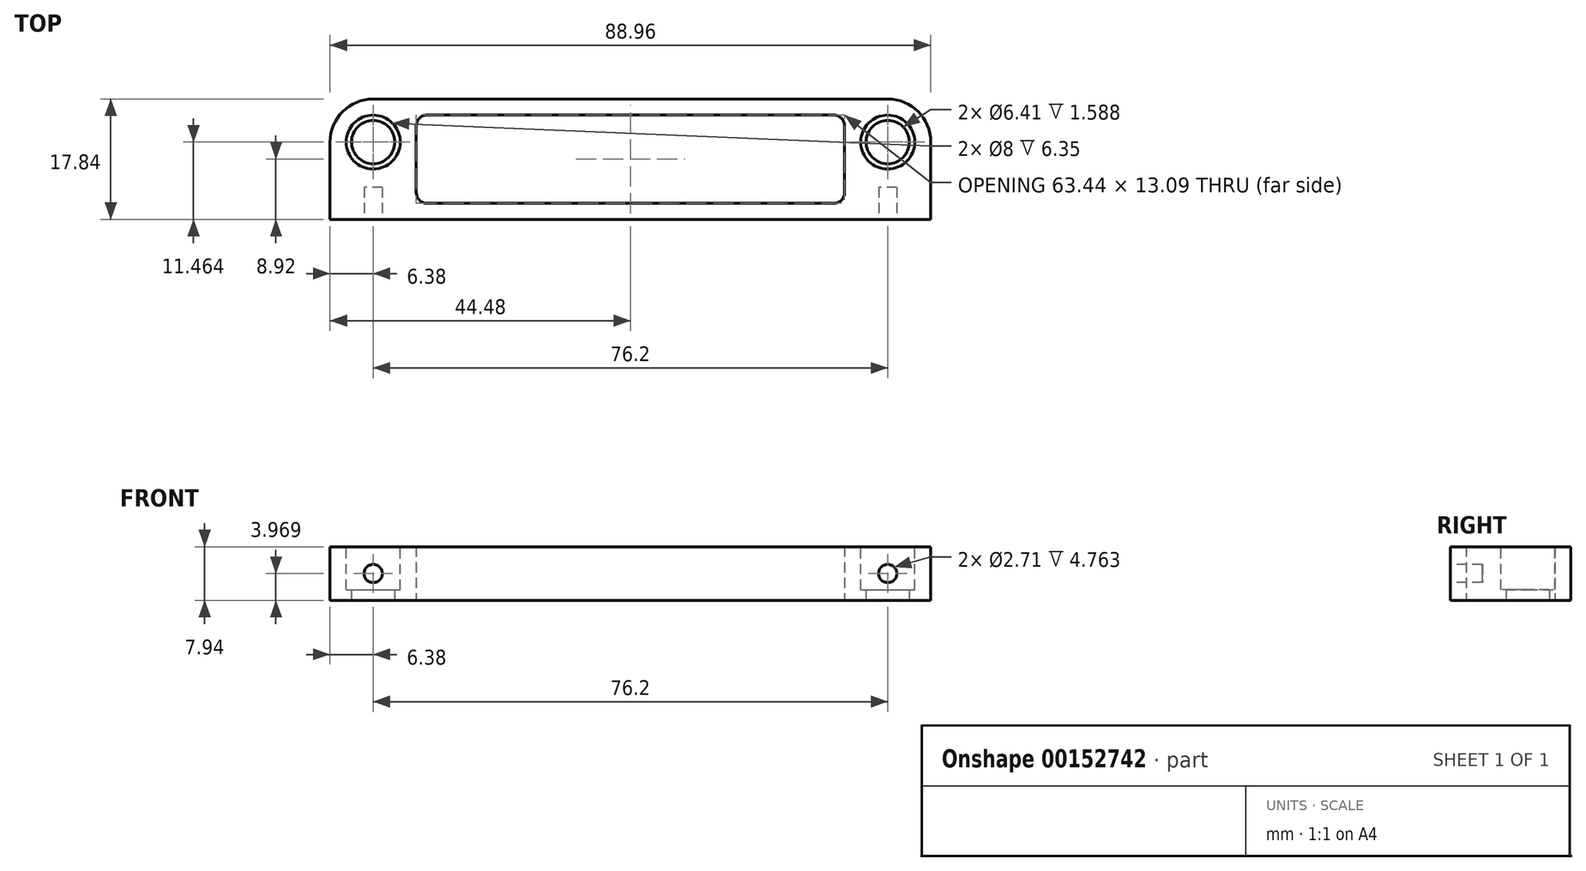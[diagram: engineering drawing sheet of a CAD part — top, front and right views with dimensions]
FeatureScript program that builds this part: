
annotation { "Feature Type Name" : "Feature", "Feature Type Description" : "" }
export const myFeature = defineFeature(function(context is Context, id is Id, definition is map)
    precondition{}
    {
        {
            var Q0;
            Q0=qCreatedBy(makeId("Top.planeOp"),FACE);
            var sketch = newSketch(context, id + "F0", { "sketchPlane" : qUnion([Q0])});
            skLineSegment(sketch, "E0.bottom", {"start": v(44.48, -8.92) * mm, "end": v(-44.48, -8.92) * mm});
            skLineSegment(sketch, "E0.top", {"start": v(44.48, 8.92) * mm, "end": v(-44.48, 8.92) * mm});
            skLineSegment(sketch, "E0.left", {"start": v(44.48, -8.92) * mm, "end": v(44.48, 8.92) * mm});
            skLineSegment(sketch, "E0.right", {"start": v(-44.48, -8.92) * mm, "end": v(-44.48, 8.92) * mm});
            skPoint(sketch, "E0.middle", {"position": v(0, 0) * mm});
            skLineSegment(sketch, "E1.bottom", {"start": v(31.72, -6.54) * mm, "end": v(-31.72, -6.54) * mm});
            skLineSegment(sketch, "E1.top", {"start": v(31.72, 6.54) * mm, "end": v(-31.72, 6.54) * mm});
            skLineSegment(sketch, "E1.left", {"start": v(31.72, -6.54) * mm, "end": v(31.72, 6.54) * mm});
            skLineSegment(sketch, "E1.right", {"start": v(-31.72, -6.54) * mm, "end": v(-31.72, 6.54) * mm});
            skLineSegment(sketch, "E2", {"start": v(44.48, 2.54) * mm, "end": v(38.1, 2.54) * mm, "construction": true});
            skLineSegment(sketch, "E3", {"start": v(38.1, 2.54) * mm, "end": v(38.1, 8.92) * mm, "construction": true});
            skCircle(sketch, "E4", {"center": v(38.1, 2.54) * mm, "radius": 3.2 * mm});
            skLineSegment(sketch, "E5", {"start": v(-44.48, 2.54) * mm, "end": v(-38.1, 2.54) * mm, "construction": true});
            skCircle(sketch, "E6", {"center": v(-38.1, 2.54) * mm, "radius": 3.2 * mm});
            skCircle(sketch, "E7", {"center": v(38.1, 2.54) * mm, "radius": 4 * mm, "construction": true});
            skLineSegment(sketch, "E8", {"start": v(38.1, 2.54) * mm, "end": v(31.72, 2.54) * mm, "construction": true});
            skSolve(sketch);
        }
        {
            var Q0;
            Q0 = qSketchRegion(id + "F0", true);
            extrude(context, id + "F1", {"entities" : qUnion([Q0]), "depth" : 7.94 * mm});
        }
        {
            var Q0;
            Q0=makeQuery(id+"F1.opExtrude","CAP_FACE",FACE,{"disambiguationData":[OSD([sQuery(id+"F0.wireOp",EDGE,"E0.bottom"),sQuery(id+"F0.wireOp",EDGE,"E0.top"),sQuery(id+"F0.wireOp",EDGE,"E0.left"),sQuery(id+"F0.wireOp",EDGE,"E0.right"),sQuery(id+"F0.wireOp",EDGE,"E1.bottom"),sQuery(id+"F0.wireOp",EDGE,"E1.top"),sQuery(id+"F0.wireOp",EDGE,"E1.left"),sQuery(id+"F0.wireOp",EDGE,"E1.right"),sQuery(id+"F0.wireOp",EDGE,"E4"),sQuery(id+"F0.wireOp",EDGE,"E6")])],"isStart":true});
            cPlane(context, id + "F2", {"entities" : qUnion([Q0]), "cplaneType" : CPlaneType.OFFSET, "offset" : 1.59 * mm, "oppositeDirection" : true, "width" : 152.4 * mm, "height" : 152.4 * mm});
        }
        {
            var Q0;
            Q0=makeQuery(id+"F1.opExtrude","CAP_FACE",FACE,{"disambiguationData":[OSD([sQuery(id+"F0.wireOp",EDGE,"E0.bottom"),sQuery(id+"F0.wireOp",EDGE,"E0.top"),sQuery(id+"F0.wireOp",EDGE,"E0.left"),sQuery(id+"F0.wireOp",EDGE,"E0.right"),sQuery(id+"F0.wireOp",EDGE,"E1.bottom"),sQuery(id+"F0.wireOp",EDGE,"E1.top"),sQuery(id+"F0.wireOp",EDGE,"E1.left"),sQuery(id+"F0.wireOp",EDGE,"E1.right"),sQuery(id+"F0.wireOp",EDGE,"E4"),sQuery(id+"F0.wireOp",EDGE,"E6")])],"isStart":false});
            var sketch = newSketch(context, id + "F3", { "sketchPlane" : qUnion([Q0])});
            skCircle(sketch, "E9", {"center": v(-38.1, 2.54) * mm, "radius": 4 * mm});
            skCircle(sketch, "E10", {"center": v(38.1, 2.54) * mm, "radius": 4 * mm});
            skSolve(sketch);
        }
        {
            var Q0;
            Q0 = qSketchRegion(id + "F3", true);
            var Q1;
            Q1=qCreatedBy(id+"F2.planeOp",FACE);
            extrude(context, id + "F4", {"entities" : qUnion([Q0]), "operationType" : NewBodyOperationType.REMOVE, "endBound" : BoundingType.UP_TO_SURFACE, "oppositeDirection" : true, "endBoundEntityFace" : qUnion([Q1]), "depth" : 25.4 * mm});
        }
        {
            var Q0;
            Q0=makeQuery(id+"F1.opExtrude","SWEPT_FACE",FACE,{"disambiguationData":[OSD([sQuery(id+"F0.wireOp",EDGE,"E0.bottom")])]});
            var sketch = newSketch(context, id + "F5", { "sketchPlane" : qUnion([Q0])});
            skLineSegment(sketch, "E11", {"start": v(-44.48, 3.97) * mm, "end": v(-38.1, 3.97) * mm, "construction": true});
            skLineSegment(sketch, "E12", {"start": v(44.48, 3.97) * mm, "end": v(38.1, 3.97) * mm, "construction": true});
            skLineSegment(sketch, "E13", {"start": v(38.1, 3.97) * mm, "end": v(38.1, 7.94) * mm, "construction": true});
            skCircle(sketch, "E14", {"center": v(-38.1, 3.97) * mm, "radius": 1.35 * mm});
            skCircle(sketch, "E15", {"center": v(38.1, 3.97) * mm, "radius": 1.35 * mm});
            skSolve(sketch);
        }
        {
            var Q0;
            Q0 = qSketchRegion(id + "F5", true);
            extrude(context, id + "F6", {"entities" : qUnion([Q0]), "operationType" : NewBodyOperationType.REMOVE, "oppositeDirection" : true, "depth" : 4.76 * mm});
        }
        {
            var Q0;
            Q0=makeQuery(id+"F1.opExtrude","SWEPT_EDGE",EDGE,{"disambiguationData":[OSD([sQuery(id+"F0.wireOp",EDGE,"E1.top"),sQuery(id+"F0.wireOp",EDGE,"E1.left")])]});
            var Q1;
            Q1=makeQuery(id+"F1.opExtrude","SWEPT_EDGE",EDGE,{"disambiguationData":[OSD([sQuery(id+"F0.wireOp",EDGE,"E1.bottom"),sQuery(id+"F0.wireOp",EDGE,"E1.left")])]});
            var Q2;
            Q2=makeQuery(id+"F1.opExtrude","SWEPT_EDGE",EDGE,{"disambiguationData":[OSD([sQuery(id+"F0.wireOp",EDGE,"E1.bottom"),sQuery(id+"F0.wireOp",EDGE,"E1.right")])]});
            var Q3;
            Q3=makeQuery(id+"F1.opExtrude","SWEPT_EDGE",EDGE,{"disambiguationData":[OSD([sQuery(id+"F0.wireOp",EDGE,"E1.top"),sQuery(id+"F0.wireOp",EDGE,"E1.right")])]});
            fillet(context, id + "F7", {"entities" : qUnion([Q0, Q1, Q2, Q3]), "radius" : 1.59 * mm, "tangentPropagation" : true, "allowEdgeOverflow" : false});
        }
        {
            var Q0;
            Q0=makeQuery(id+"F1.opExtrude","SWEPT_EDGE",EDGE,{"disambiguationData":[OSD([sQuery(id+"F0.wireOp",EDGE,"E0.top"),sQuery(id+"F0.wireOp",EDGE,"E0.left")])]});
            var Q1;
            Q1=makeQuery(id+"F1.opExtrude","SWEPT_EDGE",EDGE,{"disambiguationData":[OSD([sQuery(id+"F0.wireOp",EDGE,"E0.top"),sQuery(id+"F0.wireOp",EDGE,"E0.right")])]});
            fillet(context, id + "F8", {"entities" : qUnion([Q0, Q1]), "radius" : 6.38 * mm, "tangentPropagation" : true, "allowEdgeOverflow" : false});
        }
    });
